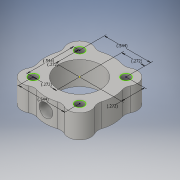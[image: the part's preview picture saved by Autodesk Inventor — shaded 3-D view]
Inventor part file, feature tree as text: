
AUTODESK INVENTOR PART (.ipt)
format: ipt  version: 2016 (Build 200138000, 138)  size: 171,008 bytes
history: native  units: in
note: dims shown in document units (in); Inventor stores cm internally (conversion verified against a paired STEP export)
features: sketch x1, fillet x1
ambient origin geometry x8: Origin, YZ Plane, XZ Plane, XY Plane, X Axis, Y Axis, Z Axis, Center Point
bodies: Solid1 (feature_tree)
feature tree (2):
  sketch  "Sketch1"  dims[d1=0.5445in d3=0.2722in d4=0.2722in d5=0.2722in d6=0.2722in d7=0.5445in]
  fillet  "Fillet1"  Radius=0.5445in
